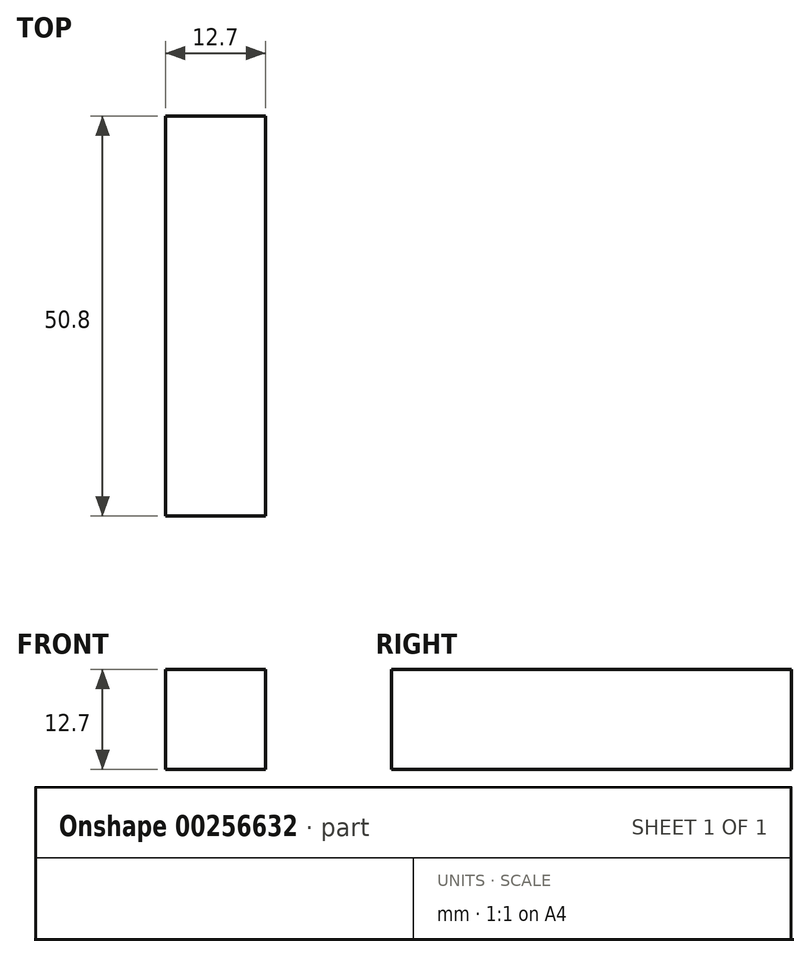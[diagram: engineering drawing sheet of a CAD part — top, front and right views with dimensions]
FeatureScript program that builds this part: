
annotation { "Feature Type Name" : "Feature", "Feature Type Description" : "" }
export const myFeature = defineFeature(function(context is Context, id is Id, definition is map)
    precondition{}
    {
        {
            var Q0;
            Q0=qCreatedBy(makeId("Front.planeOp"),FACE);
            var sketch = newSketch(context, id + "F0", { "sketchPlane" : qUnion([Q0])});
            skLineSegment(sketch, "E0.bottom", {"start": v(59.45, 34.2) * mm, "end": v(46.75, 34.2) * mm});
            skLineSegment(sketch, "E0.top", {"start": v(59.45, 21.5) * mm, "end": v(46.75, 21.5) * mm});
            skLineSegment(sketch, "E0.left", {"start": v(59.45, 34.2) * mm, "end": v(59.45, 21.5) * mm});
            skLineSegment(sketch, "E0.right", {"start": v(46.75, 34.2) * mm, "end": v(46.75, 21.5) * mm});
            skSolve(sketch);
        }
        {
            var Q0;
            Q0=makeQuery(id+"F0.imprint","IMPRINT",FACE,{"disambiguationData":[TD([[makeQuery(id+"F0.imprint","IMPRINT",EDGE,{"derivedFrom":sQuery(id+"F0.wireOp",EDGE,"E0.bottom")}),1.0]])]});
            extrude(context, id + "F1", {"entities" : qUnion([Q0]), "depth" : 50.8 * mm});
        }
    });
